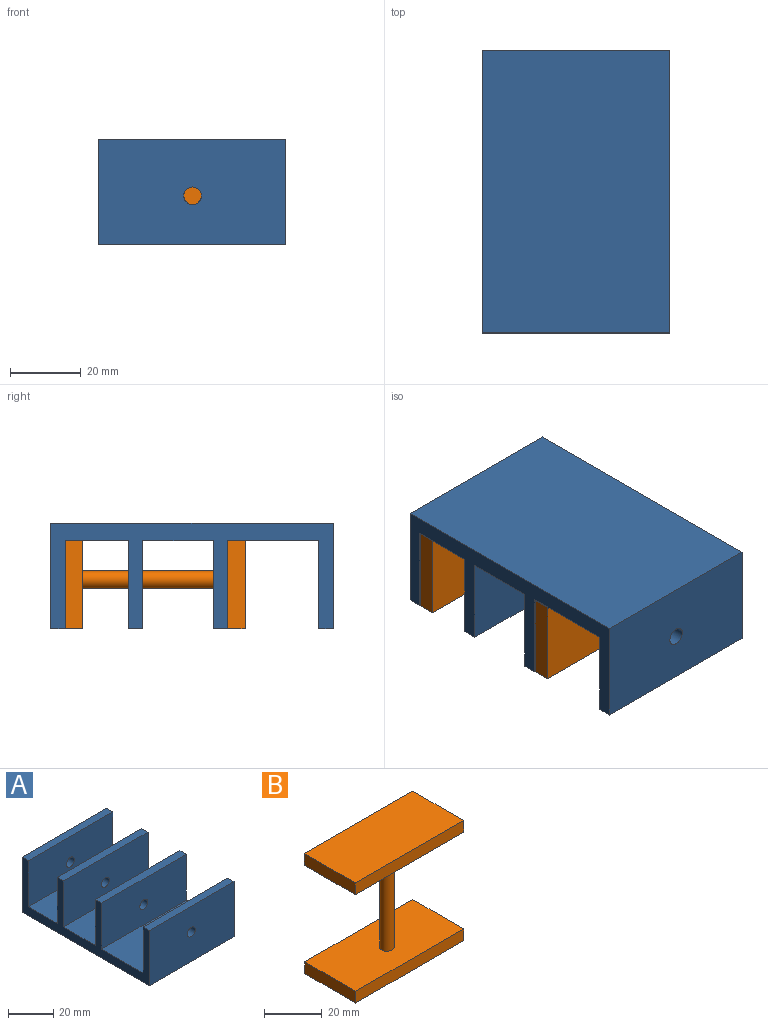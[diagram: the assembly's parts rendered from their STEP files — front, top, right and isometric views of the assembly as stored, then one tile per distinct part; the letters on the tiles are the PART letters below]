
ASSEMBLY  parts=2 mates=1
PART A: 22 faces, bbox 53.2x80x30 mm
  f0: plane 53.15x20.06mm, normal (0,0,1), area 1066.2mm2, adj f4,f6,f13,f16
  f1: plane 53.15x18.02mm, normal (0,0,1), area 957.6mm2, adj f4,f6,f8,f12
  f2: plane 53.15x25.93mm, normal (0,0,1), area 1378.4mm2, adj f4,f6,f10,f15
  f3: plane 53.15x30mm, normal (0,1,0), area 1574.9mm2, adj f4,f6,f7,f9,f21
  f4: plane 80.01x30mm, normal (-1,0,0), area 800mm2, adj f0,f1,f2,f3,f5,f7,f8,f9
  f5: plane 53.15x30mm, normal (0,-1,0), area 1574.9mm2, adj f4,f6,f7,f11,f20
  f6: plane 80.01x30mm, normal (1,0,0), area 800mm2, adj f0,f1,f2,f3,f5,f7,f8,f9
  f7: plane 80.01x53.15mm, normal (0,0,-1), area 4252.7mm2, adj f3,f4,f5,f6
  f8: plane 53.15x25mm, normal (0,-1,0), area 1309.2mm2, adj f1,f4,f6,f9,f21
  f9: plane 53.15x4mm, normal (0,0,1), area 212.6mm2, adj f3,f4,f6,f8
  f10: plane 53.15x25mm, normal (0,1,0), area 1309.2mm2, adj f2,f4,f6,f11,f20
  f11: plane 53.15x4mm, normal (0,0,1), area 212.6mm2, adj f4,f5,f6,f10
  f12: plane 53.15x25mm, normal (0,1,0), area 1309.2mm2, adj f1,f4,f6,f14,f19
  f13: plane 53.15x25mm, normal (0,-1,0), area 1309.2mm2, adj f0,f4,f6,f14,f19
  f14: plane 53.15x4mm, normal (0,0,1), area 212.6mm2, adj f4,f6,f12,f13
  f15: plane 53.15x25mm, normal (0,-1,0), area 1309.2mm2, adj f2,f4,f6,f17,f18
  f16: plane 53.15x25mm, normal (0,1,0), area 1309.2mm2, adj f0,f4,f6,f17,f18
  f17: plane 53.15x4mm, normal (0,0,1), area 212.6mm2, adj f4,f6,f15,f16
  f18: cylinder r=2.5mm len=5mm, axis (0,-1,0), area 62.8mm2, adj f15,f16
  f19: cylinder r=2.5mm len=5mm, axis (0,-1,0), area 62.8mm2, adj f12,f13
  f20: cylinder r=2.5mm len=5mm, axis (0,-1,0), area 62.8mm2, adj f5,f10
  f21: cylinder r=2.5mm len=5mm, axis (0,-1,0), area 62.8mm2, adj f3,f8
PART B: 13 faces, bbox 53.1x25.1x51.1 mm
  f0: plane 53x5mm, normal (0,1,0), area 265mm2, adj f1,f3,f4,f5
  f1: plane 25x5mm, normal (-1,0,0), area 125mm2, adj f0,f2,f4,f5
  f2: plane 53x5mm, normal (0,-1,0), area 265mm2, adj f1,f3,f4,f5
  f3: plane 25x5mm, normal (1,0,0), area 125mm2, adj f0,f2,f4,f5
  f4: plane 53x25mm, normal (0,0,1), area 1305.4mm2, adj f0,f1,f2,f3,f6
  f5: plane 53x25mm, normal (0,0,-1), area 1325mm2, adj f0,f1,f2,f3
  f6: cylinder r=2.5mm len=41.07mm, axis (0,0,-1), area 645.1mm2, adj f4,f12
  f7: plane 53.11x5mm, normal (0,1,0), area 265.6mm2, adj f8,f10,f11,f12
  f8: plane 25.02x5mm, normal (-1,0,0), area 125.1mm2, adj f7,f9,f11,f12
  f9: plane 53.11x5mm, normal (0,-1,0), area 265.6mm2, adj f8,f10,f11,f12
  f10: plane 25.02x5mm, normal (1,0,0), area 125.1mm2, adj f7,f9,f11,f12
  f11: plane 53.11x25.02mm, normal (0,0,1), area 1329.1mm2, adj f7,f8,f9,f10
  f12: plane 53.11x25.02mm, normal (0,0,-1), area 1309.4mm2, adj f6,f7,f8,f9,f10
PLACE A rot(axis=(0,1,0),180deg) t=(-60.13,-6.49,44.25)mm fixed
PLACE B rot(axis=(-1,0,0),90deg) t=(-49.02,-26.59,-7.03)mm
MATE slider A.f8 <-> B.f11  axis (0,-1,0) through (-49.64,24.48,26.73)mm
